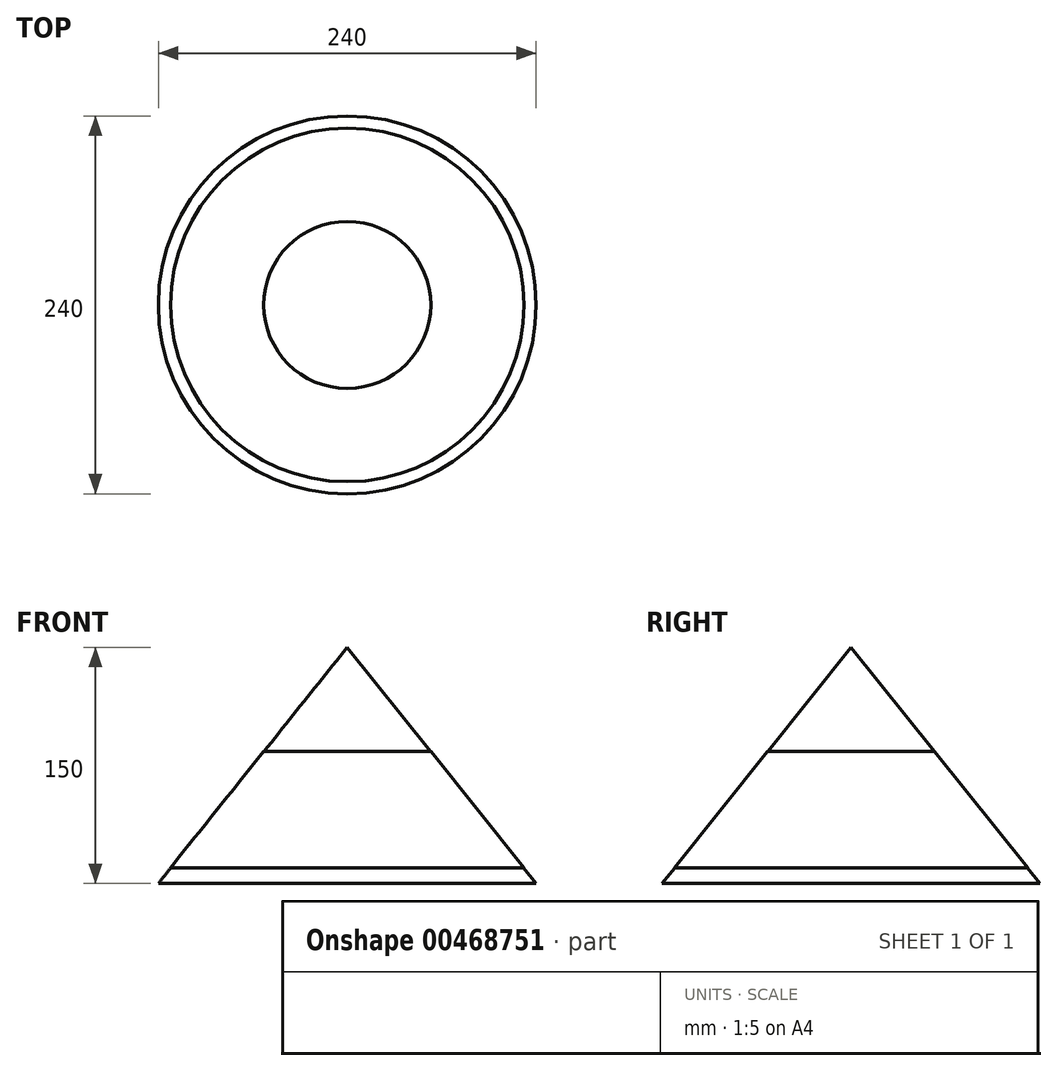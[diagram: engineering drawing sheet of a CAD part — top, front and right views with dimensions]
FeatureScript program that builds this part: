
annotation { "Feature Type Name" : "Feature", "Feature Type Description" : "" }
export const myFeature = defineFeature(function(context is Context, id is Id, definition is map)
    precondition{}
    {
        {
            var Q0;
            Q0=qCreatedBy(makeId("Front.planeOp"),FACE);
            var sketch = newSketch(context, id + "F0", { "sketchPlane" : qUnion([Q0])});
            skLineSegment(sketch, "E0.bottom", {"start": v(0, 0) * mm, "end": v(-120, 0) * mm});
            skLineSegment(sketch, "E0.left", {"start": v(0, 0) * mm, "end": v(0, 150) * mm});
            skLineSegment(sketch, "E1", {"start": v(-120, 0) * mm, "end": v(0, 150) * mm});
            skSolve(sketch);
        }
        {
            var Q0;
            Q0 = qSketchRegion(id + "F0", true);
            var Q1;
            Q1=sQuery(id+"F0.wireOp",EDGE,"E0.left");
            revolve(context, id + "F1", {"entities" : qUnion([Q0]), "axis" : qUnion([Q1]), "revolveType" : RevolveType.FULL});
        }
        {
            var Q0;
            Q0=qCreatedBy(makeId("Front.planeOp"),FACE);
            var sketch = newSketch(context, id + "F2", { "sketchPlane" : qUnion([Q0])});
            skLineSegment(sketch, "E2.0", {"start": v(0, 10) * mm, "end": v(0, 84) * mm});
            skLineSegment(sketch, "E3", {"start": v(-120, 0) * mm, "end": v(0, 150) * mm});
            skPoint(sketch, "E4.0", {"position": v(-60, 0) * mm});
            skLineSegment(sketch, "E5.0", {"start": v(0, 0) * mm, "end": v(-60, 0) * mm});
            skLineSegment(sketch, "E6.0", {"start": v(-112.26, 10) * mm, "end": v(-53.06, 84) * mm});
            skLineSegment(sketch, "E7", {"start": v(0, 84) * mm, "end": v(-53.06, 84) * mm});
            skPoint(sketch, "E8.orphan", {"position": v(-120, 0) * mm});
            skPoint(sketch, "E9.orphan", {"position": v(0, 150) * mm});
            skLineSegment(sketch, "E10.0", {"start": v(0, 10) * mm, "end": v(-112.26, 10) * mm});
            skLineSegment(sketch, "E11.trimOffspring", {"start": v(-120, 0) * mm, "end": v(-120.26, 0) * mm});
            skPoint(sketch, "E12.orphan", {"position": v(0, 0) * mm});
            skSolve(sketch);
        }
        {
            var Q0;
            Q0 = qSketchRegion(id + "F2", true);
            var Q1;
            Q1=sQuery(id+"F2.wireOp",EDGE,"E2.0");
            revolve(context, id + "F3", {"entities" : qUnion([Q0]), "axis" : qUnion([Q1]), "revolveType" : RevolveType.FULL});
        }
    });
